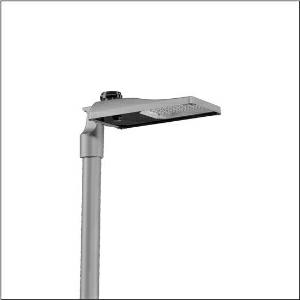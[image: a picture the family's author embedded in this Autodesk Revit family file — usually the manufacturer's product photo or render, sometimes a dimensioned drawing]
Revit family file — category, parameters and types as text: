
# Revit family: streetlight_sl_31_mini___st1_0a_5xh6d3bm08ga_d2dc
name_source: partatom
category: Lighting Fixtures
units: mm (PartAtom-declared; Revit-internal decimal feet)

## family parameters
Cut with Voids When Loaded = No
Host = Face
Light Source = No
Part Type = Normal
Room Calculation Point = No
Round Connector Dimension = Use Diameter
Shared = No

## types (1)
- --- (1 x LED, 5880 lm, 39.3 W, 3000K)
    Apparent Load = 39 VA
    CIE Flux Codes = 37 72 97 100 100
    Color Rendering = 70
    Color Temperature = 3000K
    Default Elevation = 1800 mm
    Description = Streetlight SL 31 mini NEMA (7pin) mast luminaire for post-top, side-entry; light control with lens of PMMA; light distribution: ST1.0a, direct asymmetric distribution, for standard-compliant lighting for roads and squares; LED: luminous flux: 5.880lm, light colour: 730, colour temperature: 3000K; luminous efficacy: 149,6lm/W; control: pre-setting: linear dimming characteristic, flexible luminous flux parameterisation, time-dependent luminous flux control, constant luminous flux control, intelligent temperature release in ECG and LED module, overheat protection; luminaire housing, of diecast aluminium, Siteco® metallic grey (DB 702S), corrosivity category C5 high according to DIN EN ISO 12944; cover of toughened safety glass, transparent, opened without tools; mast flange of diecast aluminium, Siteco® metallic grey (DB 702S), spigot size: 76/60mm, mast flange included unmounted; with cable H07RN-F 3x 1.5mm², cable length: 6,5m, connection cable pre-assembled; mains connection: 220..240V, AC, 50/60Hz; power consumption (at start of service life): 39,3W / (at end of service life): 40,7W / (with reduced operation 50%): 18,1W; protection rating (complete): IP66; insulation class (complete): insulation class I (protective earthing); impact resistance: IK09; certification: CE, ENEC, ENEC+, VDE, UKCA; permissible operating ambient temperature for outdoor applications: -40..+50°C; packaging unit: 1 piece

Light Distribution: ST1.0a
    Height = 76 mm
    Lamp = 1 x LED
    Lamp Light Flux = 5880 lm
    Lamp Power = 39.3 W
    Lamp count = 1
    Length = 547 mm
    Luminous efficacy = 150 lm/W
    Manufacturer = Siteco
    ModVariant = No
    Model = 5XH6D3BM08GA
    Number of Poles = 1
    OnlyDefault = Yes
    Power Factor = 1
    Product Name = Streetlight SL 31 mini | ST1.0a
    Product group = mast luminaire | pylon top
    ProductGroupID = 6100
    Protection Class = Protection class I
    Protection Degree = IP 66
    RLX_Detail_Level = 1
    RLX_Emergency_Light_Flux = 0 lm
    RLX_Emergency_Type = 0
    RLX_Emergency_Type_DB = No
    RlxData = <blob elided: 40365 chars, md5=d9576405>
    Socket = socket
    Standby Power = 0 W
    System Light Flux = 5880 lm
    System Power = 39 W
    Type Comments = factory setting: luminous flux: 100 % | dim-lin: 254 | 798 mA
    Type Image = l_1300324.jpg
    URL = http://relux.com
    VarID = @adj_074031
    Voltage = 0 V
    Weight = 0.00 kg
    Width = 265 mm

## geometry (parser evidence)
native form markers: Blend x4, Sweep x11
no freeform markers — native parametric forms only
